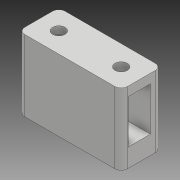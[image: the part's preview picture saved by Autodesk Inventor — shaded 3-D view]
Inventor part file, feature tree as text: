
AUTODESK INVENTOR PART (.ipt)
format: ipt  version: 2018 (Build 220112000, 112)  size: 333,824 bytes
history: native  units: mm
features: other x18, extrude x13, sketch x13, fillet x1
ambient origin geometry x8: Origin, YZ Plane, XZ Plane, XY Plane, X Axis, Y Axis, Z Axis, Center Point
bodies: Body1 (feature_tree)
feature tree (45):
  other  "Sólido1"
  extrude  "Extrusión1"  Depth=15.33mm
  extrude  "Extrusión2"  Depth=3.0mm TaperAngle=0.0deg
  extrude  "Extrusión3"  Depth=1.0mm
  extrude  "Extrusión4"  Depth=1.0mm
  extrude  "Extrusión5"  Depth=23.0mm
  extrude  "Extrusión6"  Depth=1.0mm
  extrude  "Extrusión7"  Depth=5.0mm
  extrude  "Extrusión8"  Depth=3.0mm
  extrude  "Extrusión9"  Depth=3.0mm
  extrude  "Extrusión10"  Depth=20.0mm TaperAngle=0.0deg
  extrude  "Extrusión11"  Depth=2.0mm
  fillet  "Empalme1"  Radius=3.0mm
  extrude  "Extrusión12"  Depth=3.0mm TaperAngle=0.0deg
  extrude  "Extrusión13"  Depth=3.0mm
  other  "Edición directa1"
  other  "Edición directa2"
  other  "Edición directa3"
  other  "Edición directa4"
  other  "Edición directa5"
  other  "Edición directa6"
  other  "Edición directa7"
  sketch  "Boceto1"  dims[d0=35.32mm d1=15.33mm]
  sketch  "Boceto2"  dims[d2=20.0mm d3=0.0mm d11=3.0mm d12=0.0mm]
  sketch  "Boceto3"  dims[d13=1.0mm d14=1.0mm]
  sketch  "Boceto4"  dims[d15=1.0mm d16=1.0mm]
  sketch  "Boceto5"  dims[d17=23.0mm d18=0.0mm d19=1.0mm]
  sketch  "Boceto6"  dims[d20=1.0mm d21=1.0mm]
  sketch  "Boceto7"  dims[d22=1.0mm d23=5.0mm]
  sketch  "Boceto8"  dims[d24=3.0mm d25=1.0mm]
  sketch  "Boceto9"  dims[d26=3.0mm d27=2.5mm]
  sketch  "Boceto10"  dims[d28=2.5mm d29=20.0mm d30=0.0mm]
  sketch  "Boceto11"  dims[d31=2.0mm d32=2.0mm d33=3.0mm]
  sketch  "Boceto12"  dims[d34=3.0mm d35=12.6mm d36=0.0mm]
  sketch  "Boceto13"  dims[d37=2.0mm d38=3.0mm d39=3.0mm d40=12.6mm d41=0.0mm d42=3.0mm d43=0.5mm d44=2.0mm d45=2.0mm d46=17.3mm d47=0.0mm d48=6.0mm d49=0.0mm d50=3.0mm d51=3.0mm d52=5.5mm d53=0.0mm d54=4.0mm d55=4.0mm d56=5.5mm d57=0.0mm d58=1.0mm d59=1.0mm d60=1.0mm d61=12.6mm d62=0.0mm d63=2.0mm d64=10.0mm d65=0.0mm d67=1.0mm d69=1.0mm d71=10.0mm d72=0.0mm d73=0.0mm d74=0.0mm d75=5.0mm d76=0.0mm d77=0.0mm d78=-4.75mm d79=0.0mm d80=0.0mm d81=-0.185mm d82=0.0mm d83=0.0mm d84=-1.33mm d85=0.0mm d86=0.0mm d87=-0.6mm d88=0.0mm d89=0.0mm d90=-0.6mm d91=0.0mm d92=0.0mm d93=-1.5mm d94=0.0mm d95=0.0mm d96=-1.5mm d97=0.0mm d98=0.0mm d99=-1.5mm d100=0.0mm d101=0.0mm d102=-1.5mm]
  other  "Desplazar1"
  other  "Desplazar2"
  other  "Desplazar3"
  other  "Desplazar4"
  other  "Desplazar5"
  other  "Desplazar6"
  other  "Desplazar7"
  other  "Desplazar8"
  other  "Desplazar9"
  other  "Desplazar10"
